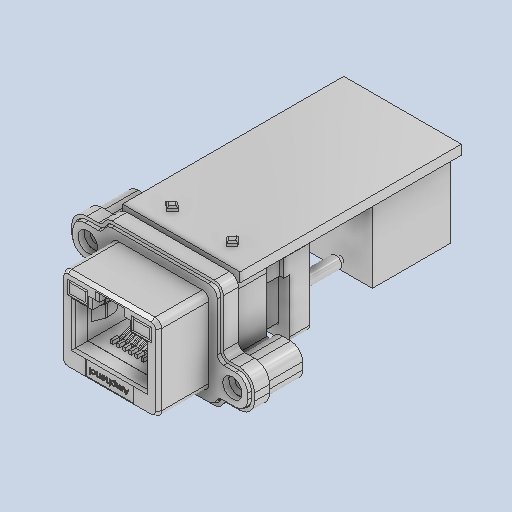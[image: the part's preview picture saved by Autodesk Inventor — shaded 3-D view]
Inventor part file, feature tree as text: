
AUTODESK INVENTOR PART (.ipt)
format: ipt  version: 2024.2 (Build 282272000, 272)  size: 968,704 bytes
history: native  units: mm
features: extrude x2, other x1
ambient origin geometry x8: Origin, YZ Plane, XZ Plane, XY Plane, X Axis, Y Axis, Z Axis, Center Point
bodies: Solid1 (feature_tree)
feature tree (3):
  extrude  "Extrusion1"  Depth=16.0mm
  extrude  "Extrusion2"  Depth=19.5mm
  other  "Boss-Extrude1"
